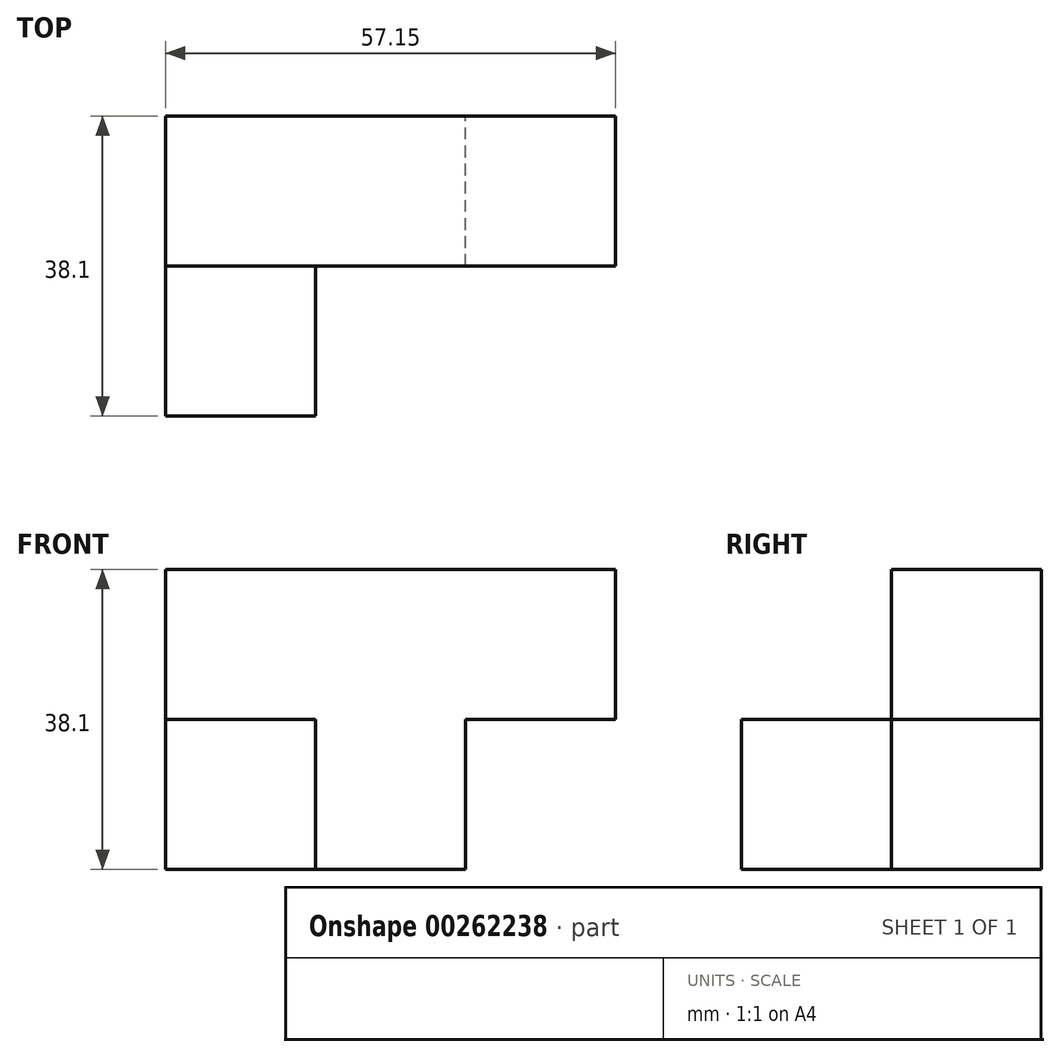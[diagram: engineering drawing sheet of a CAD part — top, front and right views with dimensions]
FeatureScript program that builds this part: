
annotation { "Feature Type Name" : "Feature", "Feature Type Description" : "" }
export const myFeature = defineFeature(function(context is Context, id is Id, definition is map)
    precondition{}
    {
        {
            var Q0;
            Q0=qCreatedBy(makeId("Front.planeOp"),FACE);
            var sketch = newSketch(context, id + "F0", { "sketchPlane" : qUnion([Q0])});
            skLineSegment(sketch, "E0.bottom", {"start": v(7.83, 47.7) * mm, "end": v(26.88, 47.7) * mm});
            skLineSegment(sketch, "E0.top", {"start": v(7.83, 28.66) * mm, "end": v(26.88, 28.66) * mm});
            skLineSegment(sketch, "E0.left", {"start": v(7.83, 47.7) * mm, "end": v(7.83, 28.66) * mm});
            skLineSegment(sketch, "E0.right", {"start": v(26.88, 47.7) * mm, "end": v(26.88, 28.66) * mm});
            skLineSegment(sketch, "E1", {"start": v(7.83, 47.7) * mm, "end": v(-11.22, 47.7) * mm});
            skLineSegment(sketch, "E2", {"start": v(7.83, 28.66) * mm, "end": v(-11.22, 28.66) * mm});
            skLineSegment(sketch, "E3", {"start": v(-11.22, 28.66) * mm, "end": v(-11.22, 47.7) * mm});
            skLineSegment(sketch, "E4", {"start": v(-11.22, 9.6) * mm, "end": v(7.83, 9.6) * mm});
            skLineSegment(sketch, "E5", {"start": v(7.83, 9.6) * mm, "end": v(26.88, 9.6) * mm});
            skLineSegment(sketch, "E6", {"start": v(26.88, 9.6) * mm, "end": v(26.88, 28.66) * mm});
            skLineSegment(sketch, "E7", {"start": v(7.83, 9.6) * mm, "end": v(7.83, 28.66) * mm});
            skLineSegment(sketch, "E8", {"start": v(-11.22, 28.66) * mm, "end": v(-11.22, 9.6) * mm});
            skLineSegment(sketch, "E9", {"start": v(26.88, 47.7) * mm, "end": v(45.93, 47.7) * mm});
            skLineSegment(sketch, "E10", {"start": v(45.93, 47.7) * mm, "end": v(45.93, 28.66) * mm});
            skLineSegment(sketch, "E11", {"start": v(45.93, 28.66) * mm, "end": v(26.88, 28.66) * mm});
            skSolve(sketch);
        }
        {
            var Q0;
            Q0=makeQuery(id+"F0.imprint","IMPRINT",FACE,{"disambiguationData":[TD([[makeQuery(id+"F0.imprint","IMPRINT",EDGE,{"derivedFrom":sQuery(id+"F0.wireOp",EDGE,"E0.bottom")}),-1.0]])]});
            var Q1;
            Q1=makeQuery(id+"F0.imprint","IMPRINT",FACE,{"disambiguationData":[TD([[makeQuery(id+"F0.imprint","IMPRINT",EDGE,{"derivedFrom":sQuery(id+"F0.wireOp",EDGE,"E0.left")}),-1.0]])]});
            var Q2;
            Q2=makeQuery(id+"F0.imprint","IMPRINT",FACE,{"disambiguationData":[TD([[makeQuery(id+"F0.imprint","IMPRINT",EDGE,{"derivedFrom":sQuery(id+"F0.wireOp",EDGE,"E0.top")}),-1.0]])]});
            var Q3;
            Q3=makeQuery(id+"F0.imprint","IMPRINT",FACE,{"disambiguationData":[TD([[makeQuery(id+"F0.imprint","IMPRINT",EDGE,{"derivedFrom":sQuery(id+"F0.wireOp",EDGE,"E0.right")}),1.0]])]});
            extrude(context, id + "F1", {"entities" : qUnion([Q0, Q1, Q2, Q3]), "depth" : 19.05 * mm});
        }
        {
            var Q0;
            Q0=makeQuery(id+"F0.imprint","IMPRINT",FACE,{"disambiguationData":[TD([[makeQuery(id+"F0.imprint","IMPRINT",EDGE,{"derivedFrom":sQuery(id+"F0.wireOp",EDGE,"E2")}),1.0]])]});
            extrude(context, id + "F2", {"entities" : qUnion([Q0]), "operationType" : NewBodyOperationType.ADD, "depth" : 38.1 * mm});
        }
    });
